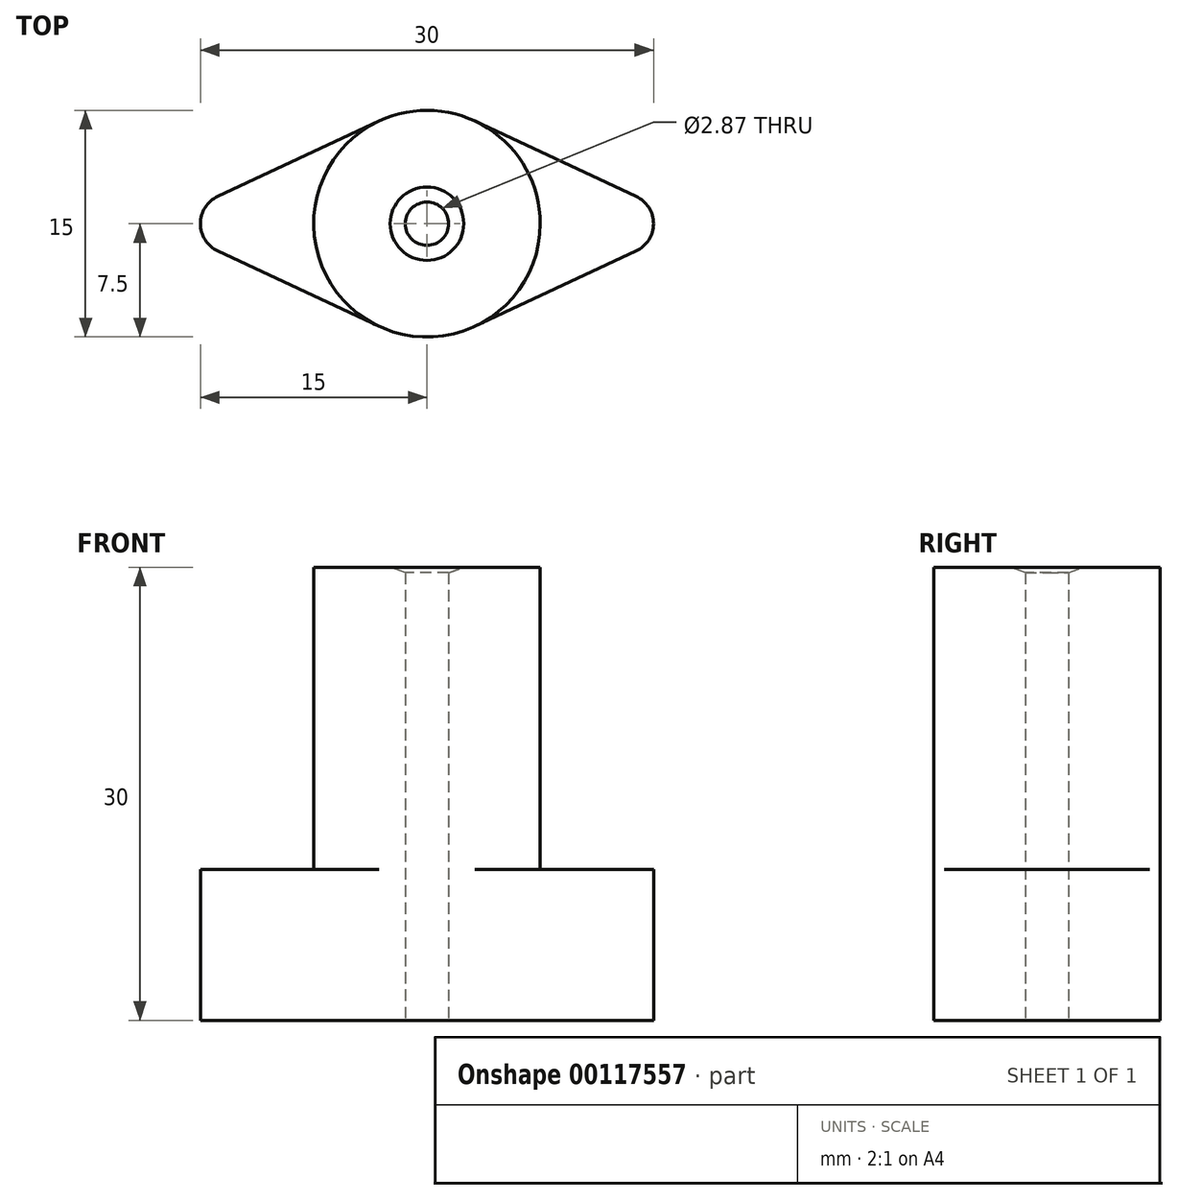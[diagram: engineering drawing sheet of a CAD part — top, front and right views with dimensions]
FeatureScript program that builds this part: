
annotation { "Feature Type Name" : "Feature", "Feature Type Description" : "" }
export const myFeature = defineFeature(function(context is Context, id is Id, definition is map)
    precondition{}
    {
        {
            var Q0;
            Q0=qCreatedBy(makeId("Top.planeOp"),FACE);
            var sketch = newSketch(context, id + "F0", { "sketchPlane" : qUnion([Q0])});
            skCircle(sketch, "E0", {"center": v(0, 0) * mm, "radius": 7.5 * mm});
            skCircle(sketch, "E1", {"center": v(0, 0) * mm, "radius": 1.44 * mm});
            skSolve(sketch);
        }
        {
            var Q0;
            Q0=qSketchRegion(id+"F0",true);
            extrude(context, id + "F1", {"entities" : qUnion([Q0]), "depth" : 30 * mm});
        }
        {
            var Q0;
            Q0=makeQuery(id+"F1.opExtrude","CAP_EDGE",EDGE,{"disambiguationData":[OSD([sQuery(id+"F0.wireOp",EDGE,"E1")])],"isStart":false});
            chamfer(context, id + "F2", {"entities" : qUnion([Q0]), "chamferType" : ChamferType.OFFSET_ANGLE, "width" : 1 * mm, "oppositeDirection" : false, "angle" : 20 * degree, "tangentPropagation" : true});
        }
        {
            var Q0;
            Q0=qCreatedBy(makeId("Top.planeOp"),FACE);
            var sketch = newSketch(context, id + "F3", { "sketchPlane" : qUnion([Q0])});
            skLineSegment(sketch, "E2", {"start": v(-3.17, 6.8) * mm, "end": v(-13.85, 1.81) * mm});
            skLineSegment(sketch, "E3", {"start": v(-13.85, -1.81) * mm, "end": v(-3.17, -6.8) * mm});
            skArc(sketch, "E4.filletArc", {"start": v(-13.85, 1.81) * mm, "mid": v(-15, 0) * mm, "end": v(-13.85, -1.81) * mm});
            skArc(sketch, "E5.0", {"start": v(-3.17, 6.8) * mm, "mid": v(-7.5, 0) * mm, "end": v(-3.17, -6.8) * mm});
            skLineSegment(sketch, "E6", {"start": v(0, 6.8) * mm, "end": v(0, -6.8) * mm, "construction": true});
            skArc(sketch, "E7.MirrorCS", {"start": v(13.85, 1.81) * mm, "mid": v(15, 0) * mm, "end": v(13.85, -1.81) * mm});
            skLineSegment(sketch, "E8.MirrorCS", {"start": v(3.17, 6.8) * mm, "end": v(13.85, 1.81) * mm});
            skArc(sketch, "E9.MirrorCS", {"start": v(3.17, 6.8) * mm, "mid": v(7.5, 0) * mm, "end": v(3.17, -6.8) * mm});
            skLineSegment(sketch, "E10.MirrorCS", {"start": v(13.85, -1.81) * mm, "end": v(3.17, -6.8) * mm});
            skSolve(sketch);
        }
        {
            var Q0;
            Q0=qSketchRegion(id+"F3",true);
            extrude(context, id + "F4", {"entities" : qUnion([Q0]), "operationType" : NewBodyOperationType.ADD, "depth" : 10 * mm});
        }
    });
